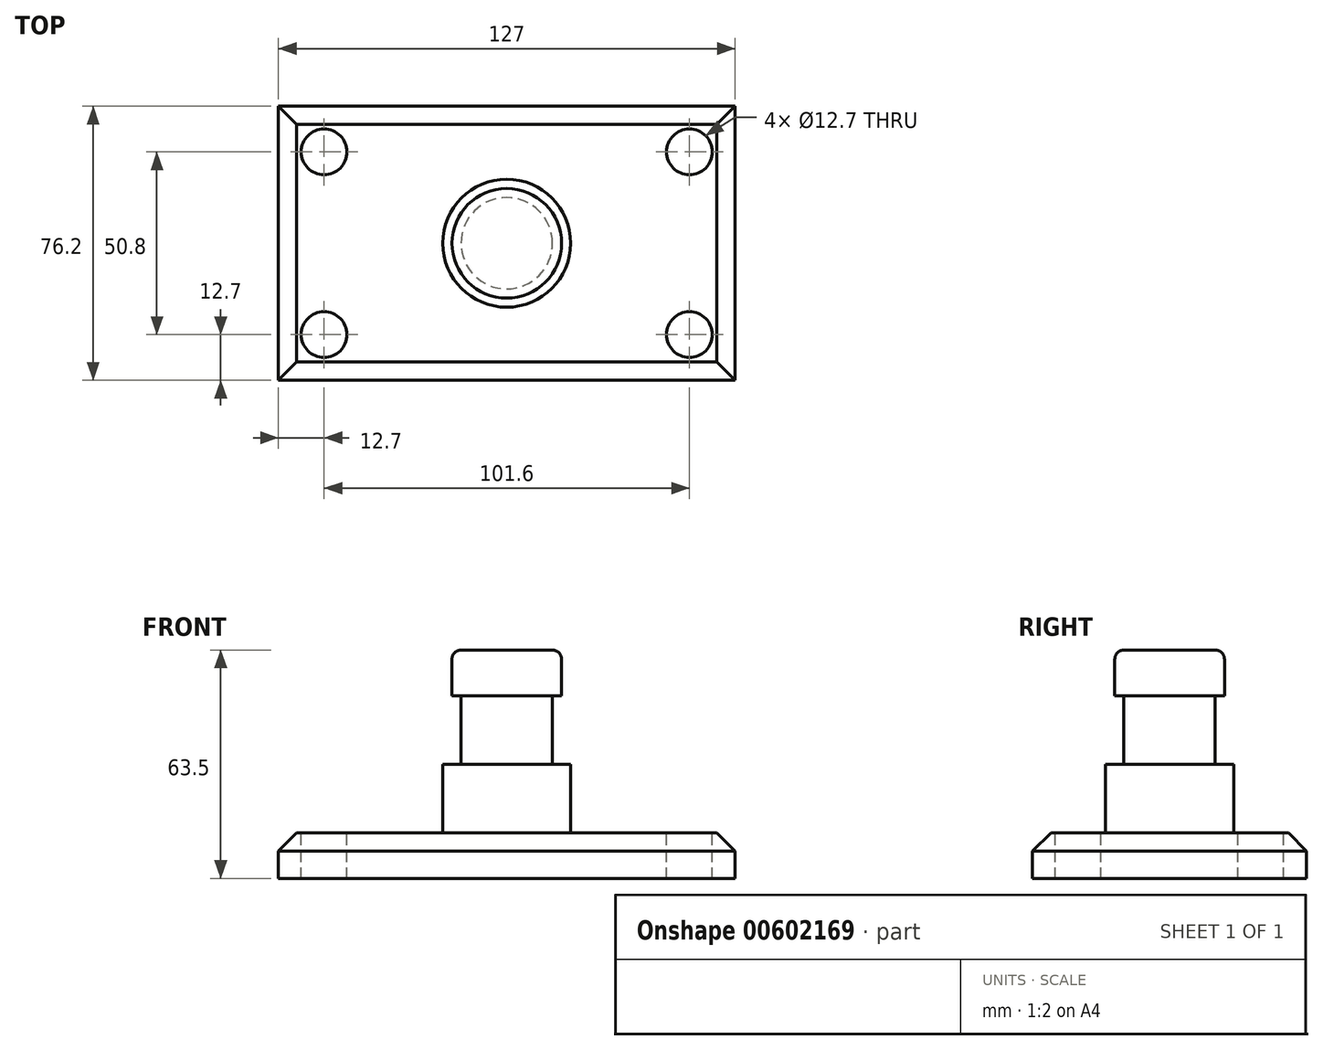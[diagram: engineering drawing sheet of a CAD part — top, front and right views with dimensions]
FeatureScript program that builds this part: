
annotation { "Feature Type Name" : "Feature", "Feature Type Description" : "" }
export const myFeature = defineFeature(function(context is Context, id is Id, definition is map)
    precondition{}
    {
        {
            var Q0;
            Q0=qCreatedBy(makeId("Top.planeOp"),FACE);
            var sketch = newSketch(context, id + "F0", { "sketchPlane" : qUnion([Q0])});
            skLineSegment(sketch, "E0.bottom", {"start": v(-63.5, 38.1) * mm, "end": v(63.5, 38.1) * mm});
            skLineSegment(sketch, "E0.top", {"start": v(-63.5, -38.1) * mm, "end": v(63.5, -38.1) * mm});
            skLineSegment(sketch, "E0.left", {"start": v(-63.5, 38.1) * mm, "end": v(-63.5, -38.1) * mm});
            skLineSegment(sketch, "E0.right", {"start": v(63.5, 38.1) * mm, "end": v(63.5, -38.1) * mm});
            skPoint(sketch, "E0.middle", {"position": v(0, 0) * mm});
            skSolve(sketch);
        }
        {
            var Q0;
            Q0=makeQuery(id+"F0.imprint","IMPRINT",FACE,{"disambiguationData":[TD([[makeQuery(id+"F0.imprint","IMPRINT",EDGE,{"derivedFrom":sQuery(id+"F0.wireOp",EDGE,"E0.bottom")}),-1.0]])]});
            extrude(context, id + "F1", {"entities" : qUnion([Q0]), "depth" : 12.7 * mm, "offsetDistance" : 25.4 * mm});
        }
        {
            var Q0;
            Q0=makeQuery(id+"F1.opExtrude","CAP_FACE",FACE,{"disambiguationData":[OSD([sQuery(id+"F0.wireOp",EDGE,"E0.bottom"),sQuery(id+"F0.wireOp",EDGE,"E0.top"),sQuery(id+"F0.wireOp",EDGE,"E0.left"),sQuery(id+"F0.wireOp",EDGE,"E0.right")])],"isStart":false});
            var sketch = newSketch(context, id + "F2", { "sketchPlane" : qUnion([Q0])});
            skLineSegment(sketch, "E1", {"start": v(-63.5, 38.1) * mm, "end": v(-50.8, 38.1) * mm});
            skLineSegment(sketch, "E2", {"start": v(-50.8, 38.1) * mm, "end": v(-50.8, 25.4) * mm});
            skSolve(sketch);
        }
        {
            var Q0;
            Q0=sQuery(id+"F2.wireOp",VERTEX,"E2.end");
            var Q1;
            Q1=makeQuery(id+"F1.opExtrude","SWEPT_BODY",BODY,{"disambiguationData":[OSD([sQuery(id+"F0.wireOp",EDGE,"E0.bottom"),sQuery(id+"F0.wireOp",EDGE,"E0.top"),sQuery(id+"F0.wireOp",EDGE,"E0.left"),sQuery(id+"F0.wireOp",EDGE,"E0.right")])]});
            hole(context, id + "F3", {"style" : HoleStyle.SIMPLE, "endStyle" : HoleEndStyle.THROUGH, "holeDiameter" : 12.7 * mm, "majorDiameter" : 6.35 * mm, "isTappedThrough" : true, "tappedDepth" : 12.7 * mm, "tapClearance" : 3, "locations" : qUnion([Q0]), "scope" : qUnion([Q1])});
        }
        {
            var Q0;
            Q0=makeQuery(id+"F1.opExtrude","CAP_FACE",FACE,{"disambiguationData":[OSD([sQuery(id+"F0.wireOp",EDGE,"E0.bottom"),sQuery(id+"F0.wireOp",EDGE,"E0.top"),sQuery(id+"F0.wireOp",EDGE,"E0.left"),sQuery(id+"F0.wireOp",EDGE,"E0.right")])],"isStart":false});
            var sketch = newSketch(context, id + "F4", { "sketchPlane" : qUnion([Q0])});
            skLineSegment(sketch, "E3", {"start": v(63.5, 38.1) * mm, "end": v(50.8, 38.1) * mm});
            skLineSegment(sketch, "E4", {"start": v(50.8, 38.1) * mm, "end": v(50.8, 25.4) * mm});
            skSolve(sketch);
        }
        {
            var Q0;
            Q0=sQuery(id+"F4.wireOp",VERTEX,"E4.end");
            var Q1;
            Q1=makeQuery(id+"F1.opExtrude","SWEPT_BODY",BODY,{"disambiguationData":[OSD([sQuery(id+"F0.wireOp",EDGE,"E0.bottom"),sQuery(id+"F0.wireOp",EDGE,"E0.top"),sQuery(id+"F0.wireOp",EDGE,"E0.left"),sQuery(id+"F0.wireOp",EDGE,"E0.right")])]});
            hole(context, id + "F5", {"style" : HoleStyle.SIMPLE, "endStyle" : HoleEndStyle.THROUGH, "holeDiameter" : 12.7 * mm, "majorDiameter" : 6.35 * mm, "isTappedThrough" : true, "tappedDepth" : 12.7 * mm, "tapClearance" : 3, "locations" : qUnion([Q0]), "scope" : qUnion([Q1])});
        }
        {
            var Q0;
            Q0=makeQuery(id+"F1.opExtrude","CAP_FACE",FACE,{"disambiguationData":[OSD([sQuery(id+"F0.wireOp",EDGE,"E0.bottom"),sQuery(id+"F0.wireOp",EDGE,"E0.top"),sQuery(id+"F0.wireOp",EDGE,"E0.left"),sQuery(id+"F0.wireOp",EDGE,"E0.right")])],"isStart":false});
            var sketch = newSketch(context, id + "F6", { "sketchPlane" : qUnion([Q0])});
            skLineSegment(sketch, "E5", {"start": v(-63.5, -38.1) * mm, "end": v(-63.5, -25.4) * mm});
            skLineSegment(sketch, "E6", {"start": v(-63.5, -25.4) * mm, "end": v(-50.8, -25.4) * mm});
            skSolve(sketch);
        }
        {
            var Q0;
            Q0=sQuery(id+"F6.wireOp",VERTEX,"E6.end");
            var Q1;
            Q1=makeQuery(id+"F1.opExtrude","SWEPT_BODY",BODY,{"disambiguationData":[OSD([sQuery(id+"F0.wireOp",EDGE,"E0.bottom"),sQuery(id+"F0.wireOp",EDGE,"E0.top"),sQuery(id+"F0.wireOp",EDGE,"E0.left"),sQuery(id+"F0.wireOp",EDGE,"E0.right")])]});
            hole(context, id + "F7", {"style" : HoleStyle.SIMPLE, "endStyle" : HoleEndStyle.THROUGH, "holeDiameter" : 12.7 * mm, "majorDiameter" : 6.35 * mm, "isTappedThrough" : true, "tappedDepth" : 12.7 * mm, "tapClearance" : 3, "locations" : qUnion([Q0]), "scope" : qUnion([Q1])});
        }
        {
            var Q0;
            Q0=makeQuery(id+"F1.opExtrude","CAP_FACE",FACE,{"disambiguationData":[OSD([sQuery(id+"F0.wireOp",EDGE,"E0.bottom"),sQuery(id+"F0.wireOp",EDGE,"E0.top"),sQuery(id+"F0.wireOp",EDGE,"E0.left"),sQuery(id+"F0.wireOp",EDGE,"E0.right")])],"isStart":false});
            var sketch = newSketch(context, id + "F8", { "sketchPlane" : qUnion([Q0])});
            skLineSegment(sketch, "E7", {"start": v(63.5, -38.1) * mm, "end": v(63.5, -25.4) * mm});
            skLineSegment(sketch, "E8", {"start": v(63.5, -25.4) * mm, "end": v(50.8, -25.4) * mm});
            skSolve(sketch);
        }
        {
            var Q0;
            Q0=sQuery(id+"F8.wireOp",VERTEX,"E8.end");
            var Q1;
            Q1=makeQuery(id+"F1.opExtrude","SWEPT_BODY",BODY,{"disambiguationData":[OSD([sQuery(id+"F0.wireOp",EDGE,"E0.bottom"),sQuery(id+"F0.wireOp",EDGE,"E0.top"),sQuery(id+"F0.wireOp",EDGE,"E0.left"),sQuery(id+"F0.wireOp",EDGE,"E0.right")])]});
            hole(context, id + "F9", {"style" : HoleStyle.SIMPLE, "endStyle" : HoleEndStyle.THROUGH, "holeDiameter" : 12.7 * mm, "majorDiameter" : 6.35 * mm, "isTappedThrough" : true, "tappedDepth" : 12.7 * mm, "tapClearance" : 3, "locations" : qUnion([Q0]), "scope" : qUnion([Q1])});
        }
        {
            var Q0;
            Q0=qCreatedBy(makeId("Front.planeOp"),FACE);
            var sketch = newSketch(context, id + "F10", { "sketchPlane" : qUnion([Q0])});
            skLineSegment(sketch, "E9.bottom", {"start": v(0, 12.7) * mm, "end": v(12.7, 12.7) * mm});
            skLineSegment(sketch, "E9.top", {"start": v(0, 63.5) * mm, "end": v(12.7, 63.5) * mm});
            skLineSegment(sketch, "E9.left", {"start": v(0, 12.7) * mm, "end": v(0, 63.5) * mm});
            skLineSegment(sketch, "E9.right", {"start": v(12.7, 12.7) * mm, "end": v(12.7, 63.5) * mm});
            skSolve(sketch);
        }
        {
            var Q0;
            Q0=makeQuery(id+"F10.imprint","IMPRINT",FACE,{"disambiguationData":[TD([[makeQuery(id+"F10.imprint","IMPRINT",EDGE,{"derivedFrom":sQuery(id+"F10.wireOp",EDGE,"E9.bottom")}),1.0]])]});
            var Q1;
            Q1=sQuery(id+"F10.wireOp",EDGE,"E9.left");
            revolve(context, id + "F11", {"operationType" : NewBodyOperationType.ADD, "entities" : qUnion([Q0]), "axis" : qUnion([Q1]), "revolveType" : RevolveType.FULL});
        }
        {
            var Q0;
            Q0=qCreatedBy(makeId("Front.planeOp"),FACE);
            var sketch = newSketch(context, id + "F12", { "sketchPlane" : qUnion([Q0])});
            skLineSegment(sketch, "E10.bottom", {"start": v(0, 31.75) * mm, "end": v(17.79, 31.75) * mm});
            skLineSegment(sketch, "E10.top", {"start": v(0, 12.7) * mm, "end": v(17.79, 12.7) * mm});
            skLineSegment(sketch, "E10.left", {"start": v(0, 31.75) * mm, "end": v(0, 12.7) * mm});
            skLineSegment(sketch, "E10.right", {"start": v(17.79, 31.75) * mm, "end": v(17.79, 12.7) * mm});
            skSolve(sketch);
        }
        {
            var Q0;
            Q0=makeQuery(id+"F12.imprint","IMPRINT",FACE,{"disambiguationData":[TD([[makeQuery(id+"F12.imprint","IMPRINT",EDGE,{"derivedFrom":sQuery(id+"F12.wireOp",EDGE,"E10.bottom")}),-1.0]])]});
            var Q1;
            Q1=sQuery(id+"F12.wireOp",EDGE,"E10.left");
            revolve(context, id + "F13", {"operationType" : NewBodyOperationType.ADD, "entities" : qUnion([Q0]), "axis" : qUnion([Q1]), "revolveType" : RevolveType.FULL});
        }
        {
            var Q0;
            Q0=qCreatedBy(makeId("Front.planeOp"),FACE);
            var sketch = newSketch(context, id + "F14", { "sketchPlane" : qUnion([Q0])});
            skLineSegment(sketch, "E11.bottom", {"start": v(0, 63.5) * mm, "end": v(15.24, 63.5) * mm});
            skLineSegment(sketch, "E11.top", {"start": v(0, 50.8) * mm, "end": v(15.24, 50.8) * mm});
            skLineSegment(sketch, "E11.left", {"start": v(0, 63.5) * mm, "end": v(0, 50.8) * mm});
            skLineSegment(sketch, "E11.right", {"start": v(15.24, 63.5) * mm, "end": v(15.24, 50.8) * mm});
            skSolve(sketch);
        }
        {
            var Q0;
            Q0=makeQuery(id+"F14.imprint","IMPRINT",FACE,{"disambiguationData":[TD([[makeQuery(id+"F14.imprint","IMPRINT",EDGE,{"derivedFrom":sQuery(id+"F14.wireOp",EDGE,"E11.bottom")}),-1.0]])]});
            var Q1;
            Q1=sQuery(id+"F14.wireOp",EDGE,"E11.left");
            revolve(context, id + "F15", {"operationType" : NewBodyOperationType.ADD, "entities" : qUnion([Q0]), "axis" : qUnion([Q1]), "revolveType" : RevolveType.FULL});
        }
        {
            var Q0;
            Q0=makeQuery(id+"F15.opRevolve","SWEPT_EDGE",EDGE,{"disambiguationData":[OSD([sQuery(id+"F14.wireOp",EDGE,"E11.bottom"),sQuery(id+"F14.wireOp",EDGE,"E11.right")])]});
            var Q1;
            Q1=makeQuery(id+"F13.opRevolve","SWEPT_EDGE",EDGE,{"disambiguationData":[OSD([sQuery(id+"F12.wireOp",EDGE,"E10.top"),sQuery(id+"F12.wireOp",EDGE,"E10.right")])]});
            fillet(context, id + "F16", {"entities" : qUnion([Q0, Q1]), "radius" : 2.54 * mm, "tangentPropagation" : true, "allowEdgeOverflow" : false});
        }
        {
            var Q0;
            Q0=makeQuery(id+"F1.opExtrude","CAP_EDGE",EDGE,{"disambiguationData":[OSD([sQuery(id+"F0.wireOp",EDGE,"E0.left")])],"isStart":false});
            var Q1;
            Q1=makeQuery(id+"F1.opExtrude","CAP_EDGE",EDGE,{"disambiguationData":[OSD([sQuery(id+"F0.wireOp",EDGE,"E0.right")])],"isStart":false});
            var Q2;
            Q2=makeQuery(id+"F1.opExtrude","CAP_EDGE",EDGE,{"disambiguationData":[OSD([sQuery(id+"F0.wireOp",EDGE,"E0.top")])],"isStart":false});
            var Q3;
            Q3=makeQuery(id+"F1.opExtrude","CAP_EDGE",EDGE,{"disambiguationData":[OSD([sQuery(id+"F0.wireOp",EDGE,"E0.bottom")])],"isStart":false});
            chamfer(context, id + "F17", {"entities" : qUnion([Q0, Q1, Q2, Q3]), "width" : 5.08 * mm, "tangentPropagation" : true});
        }
    });
